# Revit family: Вентилятор круглый шумоизолированный VS
name_source: partatom
category: Оборудование
units: mm (PartAtom-declared; Revit-internal decimal feet)

## family parameters
Всегда вертикально = Да
Заголовок OmniClass = Climate Control (HVAC)
На основе рабочей плоскости = Нет
Номер OmniClass = 23.75.00.00
Общий = Нет
При загрузке вырезать с полостями = Нет
Размер круглого соединителя = Использовать диаметр
Тип детали = Нормальный
Точка расчета площади = Нет

## types (8) — shared parameters
ADSK_Единица измерения = шт.
ADSK_Завод-изготовитель = Naveka
ADSK_Наименование = Вентилятор для круглого канала в шумоизолированном корпусе
ADSK_Примечание = https://progress-nw.ru
Материал = RAL 0000 Серый металл
Напряжение U,В = 1-220

## per-type parameters (varying)
| type | ADSK_Марка | ADSK_Масса_Текст | B | D | D+0.5 | D+4.5 | H | L | d | Мощность двигателя N,Вт | Сила тока J, А | Частота вращения n, об/мин |
| VS-100 | VS-100 | 10.8 кг | 350 мм | 49 мм | 50 мм | 54 мм | 225 мм | 460 мм | 100 мм | 70 | 0.3 | 2500 |
| VS-125 | VS-125 | 11.5 кг | 390 мм | 62 мм | 62 мм | 66 мм | 225 мм | 460 мм | 125 мм | 70 | 0.3 | 2400 |
| VS-160 | VS-160 | 12.7 кг | 420 мм | 79 мм | 80 мм | 84 мм | 260 мм | 500 мм | 160 мм | 115 | 0.5 | 2550 |
| VS-200 | VS-200 | 13.6 кг | 450 мм | 99 мм | 100 мм | 104 мм | 300 мм | 500 мм | 200 мм | 150 | 0.7 | 2600 |
| VS-250 | VS-250 | 15.0 кг | 500 мм | 124 мм | 125 мм | 129 мм | 350 мм | 550 мм | 250 мм | 200 | 0.9 | 2500 |
| VS-315A | VS-315A | 17.1 кг | 550 мм | 157 мм | 157 мм | 161 мм | 400 мм | 600 мм | 315 мм | 250 | 1.1 | 2400 |
| VS-315B | VS-315B | 17.1 кг | 550 мм | 157 мм | 157 мм | 161 мм | 400 мм | 600 мм | 315 мм | 225 | 1.0 | 2700 |
| VS(EC)-200 | VS-200 | 9.3 кг | 500 мм | 99 мм | 100 мм | 104 мм | 300 мм | 500 мм | 200 мм | 230 | 1.8 | 2400 |
